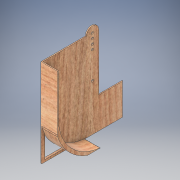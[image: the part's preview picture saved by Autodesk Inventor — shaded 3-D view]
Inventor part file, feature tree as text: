
AUTODESK INVENTOR PART (.ipt)
format: ipt  version: 2019 (Build 230136000, 136)  size: 225,792 bytes
history: native  units: in
note: dims shown in document units (in); Inventor stores cm internally (conversion verified against a paired STEP export)
features: extrude x5, sketch x4, hole x2, pattern_linear x2, chamfer x2
ambient origin geometry x8: Origin, YZ Plane, XZ Plane, XY Plane, X Axis, Y Axis, Z Axis, Center Point
bodies: Solid1 (feature_tree)
feature tree (15):
  extrude  "Extrusion1"  Depth=4.5in
  sketch  "Sketch2"  dims[d2=3.7402in d3=0.5in]
  hole  "Hole2"  [1 undecoded]
  hole  "Hole3"  [1 undecoded]
  pattern_linear  "Rectangular Pattern1"  Spacing1=2.5in  [1 undecoded]
  extrude  "Extrusion2"  Depth=0.0787in
  extrude  "Extrusion3"  Depth=3.7402in
  extrude  "Extrusion4"  Depth=3.7402in
  chamfer  "Chamfer1"  Distance=4.0in
  pattern_linear  "Rectangular Pattern2"  Spacing1=0.25in  [1 undecoded]
  extrude  "Extrusion6"  Depth=0.0787in
  chamfer  "Chamfer2"  Distance=0.0787in
  sketch  "Sketch1"  dims[d0=7.0787in d1=4.5in]
  sketch  "Sketch4"  dims[d4=2.9528in d5=0.3858in]
  sketch  "Sketch9"  dims[d6=0.0in d8=2.5in d9=2.0in d10=3.7402in d11=3.7402in d12=4.0in d13=0.25in d14=0.25in d17=0.0787in d18=0.0in d19=4.0in d20=3.7402in d21=2.9528in d29=0.1772in d30=0.75in d31=0.375in d32=0.25in d33=0.5635in d34=1.0in d35=0.8108in d36=0.1772in d37=0.75in d38=0.375in d39=0.25in d40=0.5635in d41=1.0in d42=0.8108in d43=1.1811in d45=0.3858in d46=2.0in d47=90.0deg d48=0.0787in d49=1.3287in d50=0.0in d51=3.7402in d52=3.7402in d53=3.7402in d54=180.0deg d55=90.0deg d56=4.0in d57=1.25in d58=0.0in d59=1.4469in d60=0.0in d61=0.4in d62=0.125in d63=150.0deg d75=0.7874in d77=0.3858in d126=0.0787in d127=2.5591in d128=0.0787in d129=0.0in d130=0.0787in d131=0.0787in d132=45.0deg]
note: 4 required parameter values undecoded (feature->parameter linkage not recoverable at this tier; creation-order binding heuristic only, values carry confidence <= 0.55)
